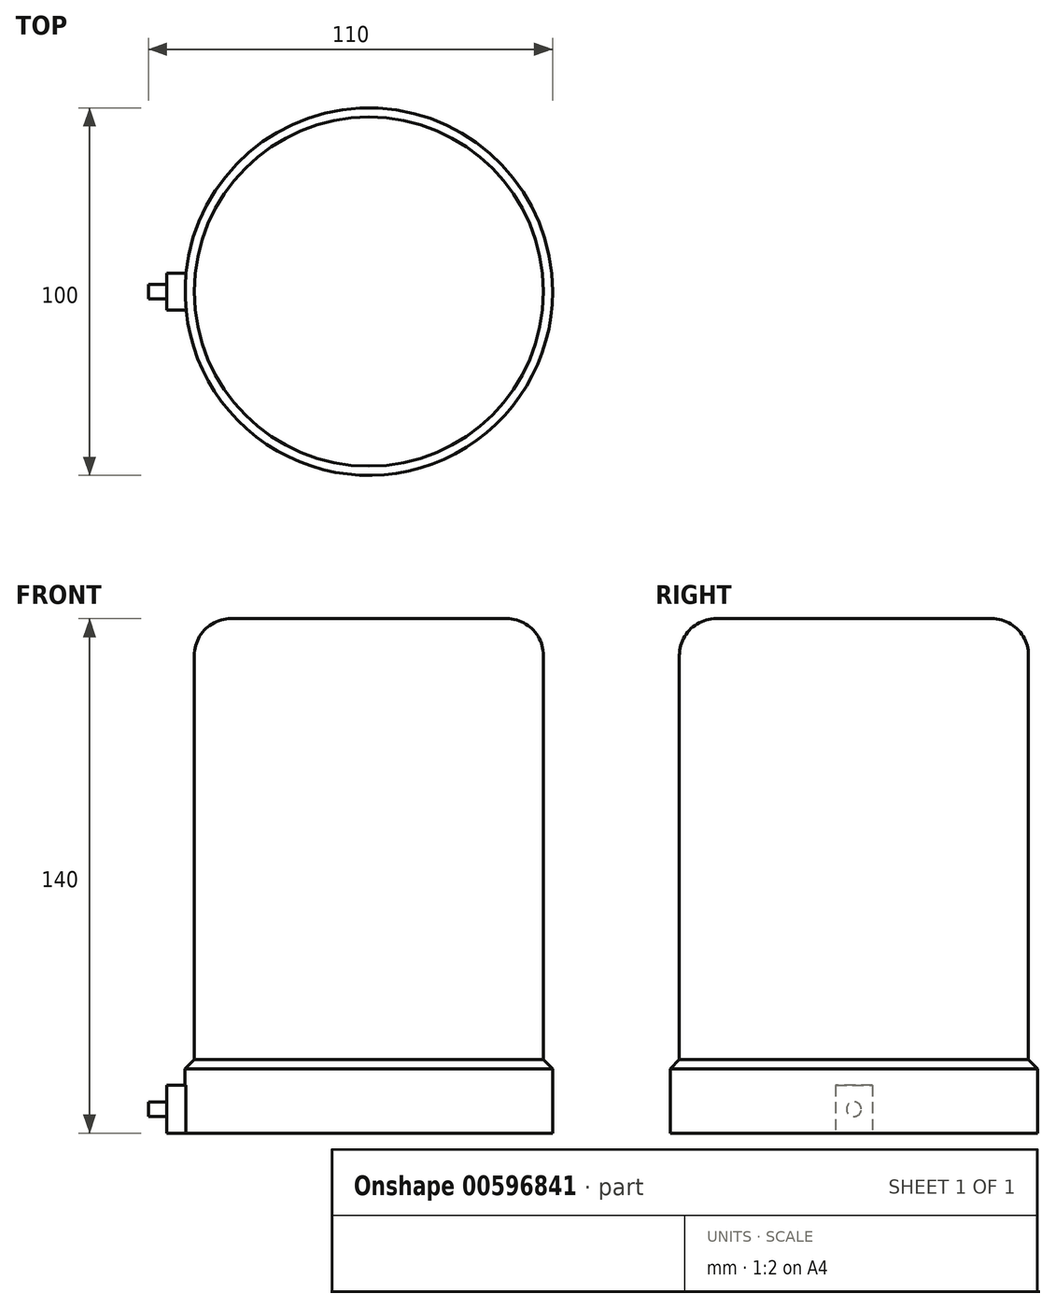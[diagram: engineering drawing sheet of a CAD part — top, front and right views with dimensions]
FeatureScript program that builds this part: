
annotation { "Feature Type Name" : "Feature", "Feature Type Description" : "" }
export const myFeature = defineFeature(function(context is Context, id is Id, definition is map)
    precondition{}
    {
        {
            var Q0;
            Q0=qCreatedBy(makeId("Top.planeOp"),FACE);
            var sketch = newSketch(context, id + "F0", { "sketchPlane" : qUnion([Q0])});
            skCircle(sketch, "E0", {"center": v(0, 0) * mm, "radius": 50 * mm});
            skSolve(sketch);
        }
        {
            var Q0;
            Q0 = qSketchRegion(id + "F0", true);
            extrude(context, id + "F1", {"entities" : qUnion([Q0]), "depth" : 20 * mm, "offsetDistance" : 25 * mm});
        }
        {
            var Q0;
            Q0=makeQuery(id+"F1.opExtrude","CAP_FACE",FACE,{"disambiguationData":[OSD([sQuery(id+"F0.wireOp",EDGE,"E0")])],"isStart":false});
            var sketch = newSketch(context, id + "F2", { "sketchPlane" : qUnion([Q0])});
            skCircle(sketch, "E1", {"center": v(0, 0) * mm, "radius": 47.5 * mm});
            skSolve(sketch);
        }
        {
            var Q0;
            Q0=makeQuery(id+"F2.imprint","IMPRINT",FACE,{"disambiguationData":[TD([[makeQuery(id+"F2.imprint","IMPRINT",EDGE,{"derivedFrom":sQuery(id+"F2.wireOp",EDGE,"E1")}),1.0]])]});
            extrude(context, id + "F3", {"entities" : qUnion([Q0]), "operationType" : NewBodyOperationType.ADD, "depth" : 120 * mm, "offsetDistance" : 25 * mm});
        }
        {
            var Q0;
            Q0=makeQuery(id+"F3.opExtrude","CAP_EDGE",EDGE,{"disambiguationData":[OSD([sQuery(id+"F2.wireOp",EDGE,"E1")])],"isStart":false});
            fillet(context, id + "F4", {"entities" : qUnion([Q0]), "radius" : 10 * mm, "tangentPropagation" : true, "allowEdgeOverflow" : false});
        }
        {
            var Q0;
            Q0=makeQuery(id+"F1.opExtrude","CAP_EDGE",EDGE,{"disambiguationData":[OSD([sQuery(id+"F0.wireOp",EDGE,"E0")])],"isStart":false});
            chamfer(context, id + "F5", {"entities" : qUnion([Q0]), "width" : 2.5 * mm, "tangentPropagation" : true});
        }
        {
            var Q0;
            Q0=makeQuery(id+"F1.opExtrude","CAP_FACE",FACE,{"disambiguationData":[OSD([sQuery(id+"F0.wireOp",EDGE,"E0")])],"isStart":true});
            var sketch = newSketch(context, id + "F6", { "sketchPlane" : qUnion([Q0])});
            skLineSegment(sketch, "E2.bottom", {"start": v(-55, 0) * mm, "end": v(0, 0) * mm});
            skLineSegment(sketch, "E2.top", {"start": v(-55, 5) * mm, "end": v(0, 5) * mm});
            skLineSegment(sketch, "E2.left", {"start": v(-55, 0) * mm, "end": v(-55, 5) * mm});
            skLineSegment(sketch, "E2.right", {"start": v(0, 0) * mm, "end": v(0, 5) * mm});
            skLineSegment(sketch, "E3.bottom", {"start": v(0, 0) * mm, "end": v(-55, 0) * mm});
            skLineSegment(sketch, "E3.top", {"start": v(0, -5) * mm, "end": v(-55, -5) * mm});
            skLineSegment(sketch, "E3.left", {"start": v(0, 0) * mm, "end": v(0, -5) * mm});
            skLineSegment(sketch, "E3.right", {"start": v(-55, 0) * mm, "end": v(-55, -5) * mm});
            skSolve(sketch);
        }
        {
            var Q0;
            {var subQ0=sQuery(id+"F6.wireOp",EDGE,"E3.right");Q0=makeQuery(id+"F6.imprint","IMPRINT",FACE,{"disambiguationData":[TD([[makeQuery(id+"F6.imprint","IMPRINT",EDGE,{"derivedFrom":subQ0}),1.0]])]});}
            var Q1;
            {var subQ0=sQuery(id+"F6.wireOp",EDGE,"E2.left");Q1=makeQuery(id+"F6.imprint","IMPRINT",FACE,{"disambiguationData":[TD([[makeQuery(id+"F6.imprint","IMPRINT",EDGE,{"derivedFrom":subQ0}),-1.0]])]});}
            extrude(context, id + "F7", {"entities" : qUnion([Q0, Q1]), "operationType" : NewBodyOperationType.ADD, "oppositeDirection" : true, "depth" : 13 * mm, "offsetDistance" : 25 * mm});
        }
        {
            var Q0;
            Q0=makeQuery(id+"F7.opExtrude","SWEPT_FACE",FACE,{"disambiguationData":[OSD([sQuery(id+"F6.wireOp",EDGE,"E2.left"),sQuery(id+"F6.wireOp",EDGE,"E3.right")])]});
            var sketch = newSketch(context, id + "F8", { "sketchPlane" : qUnion([Q0])});
            skCircle(sketch, "E4", {"center": v(0, 6.5) * mm, "radius": 2 * mm});
            skPoint(sketch, "E4.centerSnap0", {"position": v(0, 13) * mm});
            skPoint(sketch, "E4.centerSnap1", {"position": v(5, 6.5) * mm});
            skSolve(sketch);
        }
        {
            var Q0;
            Q0=makeQuery(id+"F8.imprint","IMPRINT",FACE,{"disambiguationData":[TD([[makeQuery(id+"F8.imprint","IMPRINT",EDGE,{"derivedFrom":sQuery(id+"F8.wireOp",EDGE,"E4")}),1.0]])]});
            extrude(context, id + "F9", {"entities" : qUnion([Q0]), "operationType" : NewBodyOperationType.ADD, "depth" : 5 * mm, "offsetDistance" : 25 * mm});
        }
    });
